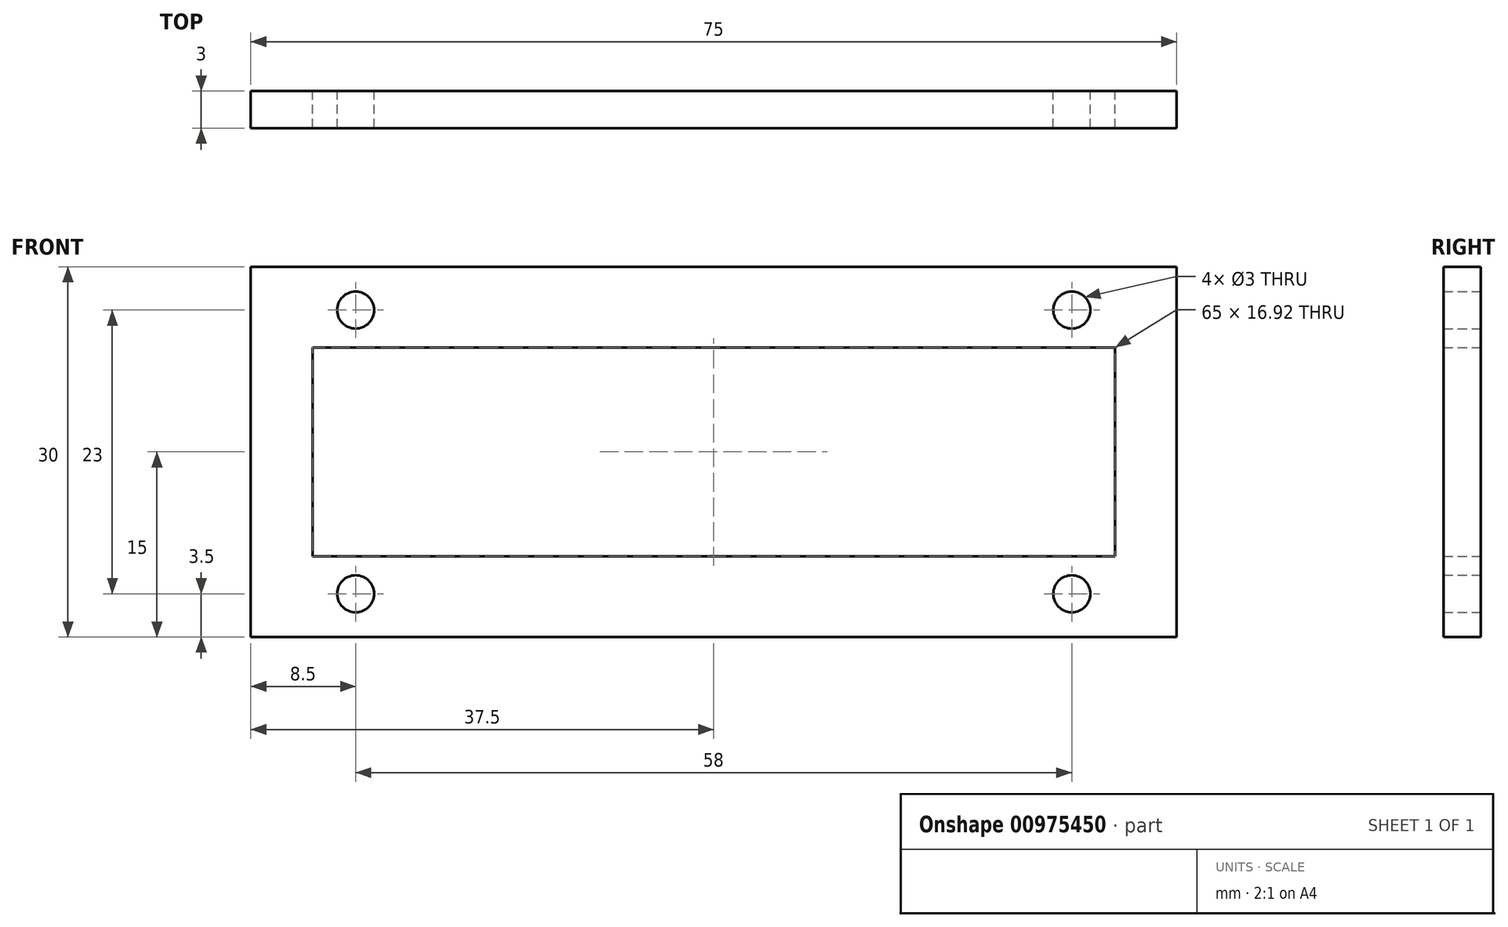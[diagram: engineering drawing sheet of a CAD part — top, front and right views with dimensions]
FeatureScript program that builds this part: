
annotation { "Feature Type Name" : "Feature", "Feature Type Description" : "" }
export const myFeature = defineFeature(function(context is Context, id is Id, definition is map)
    precondition{}
    {
        {
            var Q0;
            Q0=qCreatedBy(makeId("Front.planeOp"),FACE);
            var sketch = newSketch(context, id + "F0", { "sketchPlane" : qUnion([Q0])});
            skPoint(sketch, "E0.middle", {"position": v(0, 0) * mm});
            skCircle(sketch, "E1", {"center": v(-29, 11.5) * mm, "radius": 1.5 * mm});
            skCircle(sketch, "E2", {"center": v(-29, -11.5) * mm, "radius": 1.5 * mm});
            skCircle(sketch, "E3", {"center": v(29, -11.5) * mm, "radius": 1.5 * mm});
            skCircle(sketch, "E4", {"center": v(29, 11.5) * mm, "radius": 1.5 * mm});
            skLineSegment(sketch, "E5.bottom", {"start": v(37.5, 15) * mm, "end": v(-37.5, 15) * mm});
            skLineSegment(sketch, "E5.top", {"start": v(37.5, -15) * mm, "end": v(-37.5, -15) * mm});
            skLineSegment(sketch, "E5.left", {"start": v(37.5, 15) * mm, "end": v(37.5, -15) * mm});
            skLineSegment(sketch, "E5.right", {"start": v(-37.5, 15) * mm, "end": v(-37.5, -15) * mm});
            skLineSegment(sketch, "E6.bottom", {"start": v(32.5, 8.46) * mm, "end": v(-32.5, 8.46) * mm});
            skLineSegment(sketch, "E6.top", {"start": v(32.5, -8.46) * mm, "end": v(-32.5, -8.46) * mm});
            skLineSegment(sketch, "E6.left", {"start": v(32.5, 8.46) * mm, "end": v(32.5, -8.46) * mm});
            skLineSegment(sketch, "E6.right", {"start": v(-32.5, 8.46) * mm, "end": v(-32.5, -8.46) * mm});
            skSolve(sketch);
        }
        {
            var Q0;
            Q0=makeQuery(id+"F0.imprint","IMPRINT",FACE,{"disambiguationData":[TD([[makeQuery(id+"F0.imprint","IMPRINT",EDGE,{"derivedFrom":sQuery(id+"F0.wireOp",EDGE,"E1")}),-1.0]])]});
            extrude(context, id + "F1", {"entities" : qUnion([Q0]), "depth" : 3 * mm, "offsetDistance" : 25 * mm});
        }
    });
